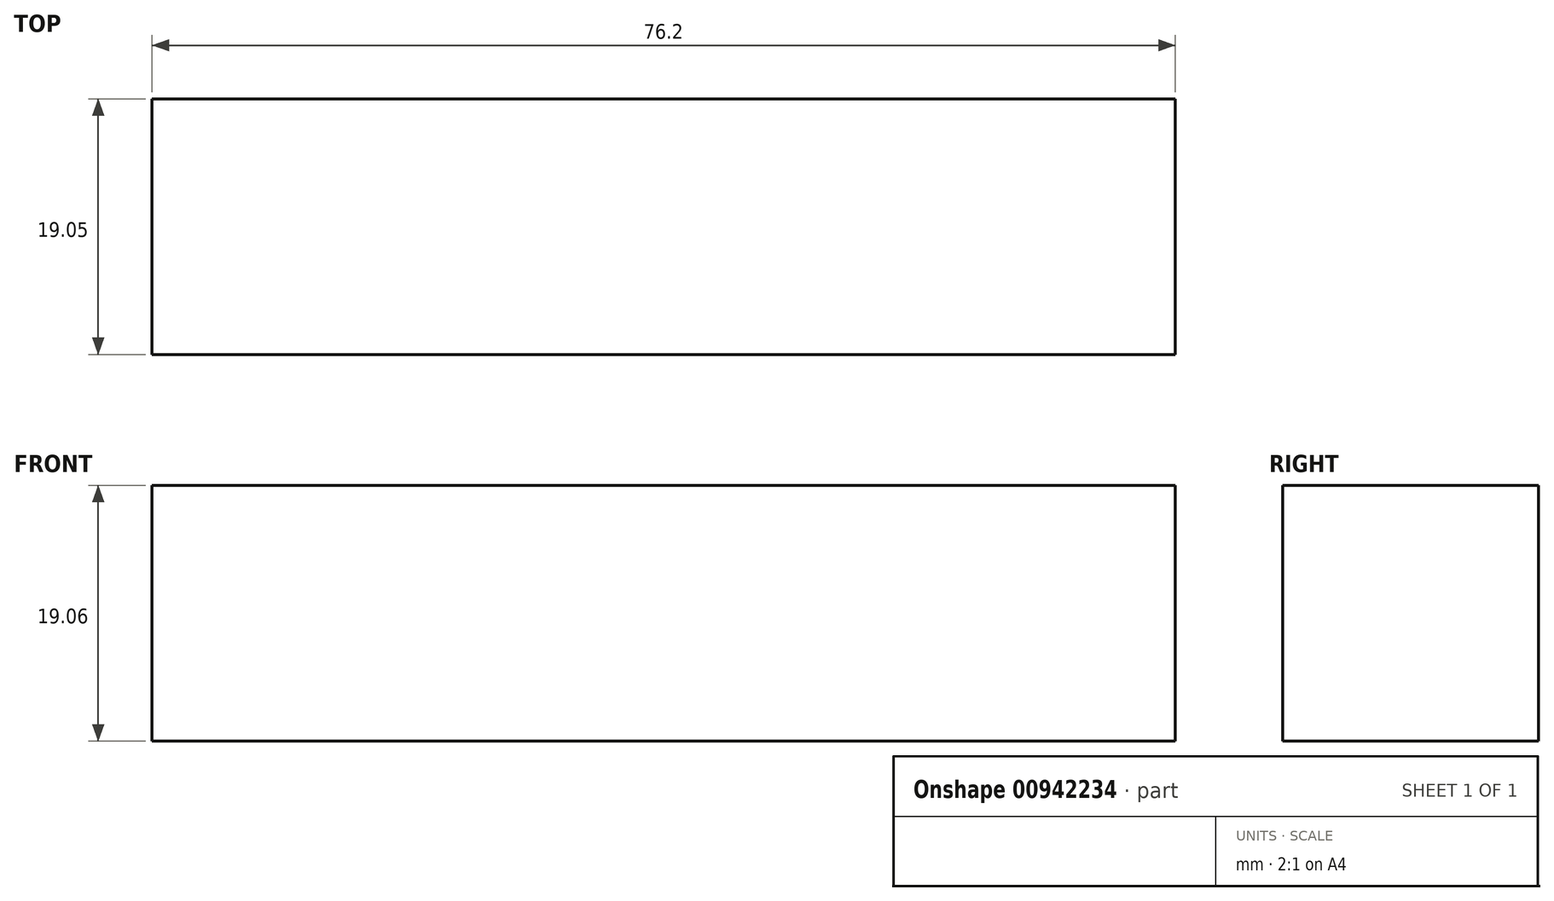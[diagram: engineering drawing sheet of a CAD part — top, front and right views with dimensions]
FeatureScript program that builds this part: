
annotation { "Feature Type Name" : "Feature", "Feature Type Description" : "" }
export const myFeature = defineFeature(function(context is Context, id is Id, definition is map)
    precondition{}
    {
        {
            var Q0;
            Q0=qCreatedBy(makeId("Front.planeOp"),FACE);
            var sketch = newSketch(context, id + "F0", { "sketchPlane" : qUnion([Q0])});
            skLineSegment(sketch, "E0.bottom", {"start": v(38.1, 9.53) * mm, "end": v(-38.1, 9.53) * mm});
            skLineSegment(sketch, "E0.top", {"start": v(38.1, -9.53) * mm, "end": v(-38.1, -9.53) * mm});
            skLineSegment(sketch, "E0.left", {"start": v(38.1, 9.53) * mm, "end": v(38.1, -9.53) * mm});
            skLineSegment(sketch, "E0.right", {"start": v(-38.1, 9.53) * mm, "end": v(-38.1, -9.53) * mm});
            skPoint(sketch, "E0.middle", {"position": v(0, 0) * mm});
            skSolve(sketch);
        }
        {
            var Q0;
            Q0 = qSketchRegion(id + "F0", true);
            extrude(context, id + "F1", {"entities" : qUnion([Q0]), "depth" : 19.05 * mm, "offsetDistance" : 25.4 * mm});
        }
    });
